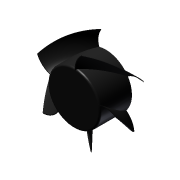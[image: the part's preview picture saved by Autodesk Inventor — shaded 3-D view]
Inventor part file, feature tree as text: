
AUTODESK INVENTOR PART (.ipt)
format: ipt  version: 2014 (Build 180170000, 170)  size: 239,616 bytes
history: native  units: mm (DEFAULTED — no unit token found)
features: sketch x2, extrude x1, fillet x1, other x1, helix x1, pattern_circular x1
ambient origin geometry x8: Origin, YZ Plane, XZ Plane, XY Plane, X Axis, Y Axis, Z Axis, Center Point
bodies: Solid1 (feature_tree)
feature tree (7):
  extrude  "Extrusion1"  Depth=0.79375mm
  fillet  "Fillet1"  Radius=0.3175mm
  sketch  "Sketch2"  dims[d5=0.698132mm d6=8.89mm d7=37.338mm d8=127.0mm d9=14.3002mm d10=1.5mm d11=0.0mm d12=90.0deg d13=90.0deg d14=0.0mm d15=0.0mm d16=50.0mm d18=360.0deg]
  other  "Work Axis1"
  helix  "Coil1"  [1 undecoded]
  pattern_circular  "Circular Pattern1"  [2 undecoded]
  sketch  "Sketch1"  dims[d0=14.3002mm d1=0.0mm d2=0.79375mm d3=0.3175mm d4=2.094086mm]
note: 3 required parameter values undecoded (feature->parameter linkage not recoverable at this tier; creation-order binding heuristic only, values carry confidence <= 0.55)
